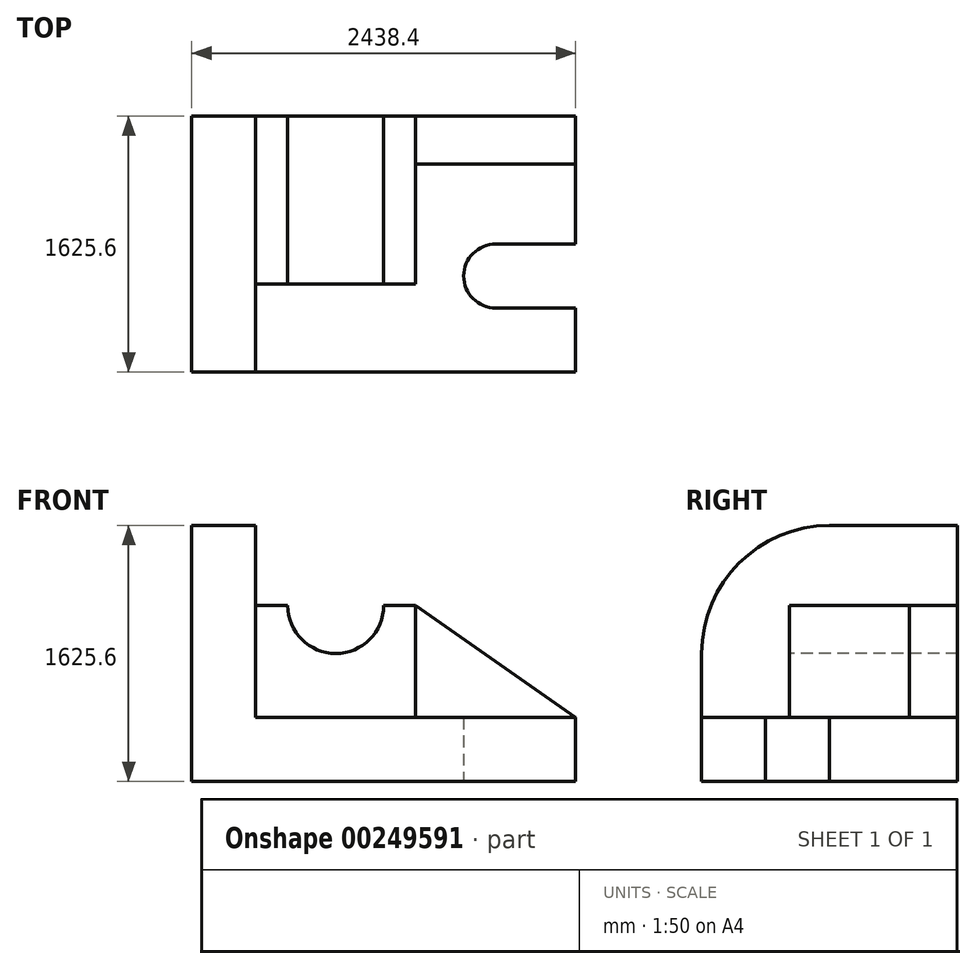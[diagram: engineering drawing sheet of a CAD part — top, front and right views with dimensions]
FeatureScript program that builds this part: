
annotation { "Feature Type Name" : "Feature", "Feature Type Description" : "" }
export const myFeature = defineFeature(function(context is Context, id is Id, definition is map)
    precondition{}
    {
        {
            var Q0;
            Q0=qCreatedBy(makeId("Top.planeOp"),FACE);
            var sketch = newSketch(context, id + "F0", { "sketchPlane" : qUnion([Q0])});
            skLineSegment(sketch, "E0.bottom", {"start": v(0, 0) * mm, "end": v(-2438.4, 0) * mm});
            skLineSegment(sketch, "E0.top", {"start": v(0, 1625.6) * mm, "end": v(-2438.4, 1625.6) * mm});
            skLineSegment(sketch, "E0.left", {"start": v(0, 0) * mm, "end": v(0, 1625.6) * mm});
            skLineSegment(sketch, "E0.right", {"start": v(-2438.4, 0) * mm, "end": v(-2438.4, 1625.6) * mm});
            skLineSegment(sketch, "E1", {"start": v(0, 0) * mm, "end": v(0, 406.4) * mm});
            skLineSegment(sketch, "E2", {"start": v(0, 406.4) * mm, "end": v(-508, 406.4) * mm});
            skLineSegment(sketch, "E3", {"start": v(-508, 812.8) * mm, "end": v(0, 812.8) * mm});
            skArc(sketch, "E4", {"start": v(-508, 812.8) * mm, "mid": v(-711.2, 609.6) * mm, "end": v(-508, 406.4) * mm});
            skLineSegment(sketch, "E5.bottom", {"start": v(0, 1625.6) * mm, "end": v(-863.6, 1625.6) * mm});
            skLineSegment(sketch, "E5.left", {"start": v(0, 1625.6) * mm, "end": v(0, 1320.8) * mm});
            skSolve(sketch);
        }
        {
            var Q0;
            Q0=makeQuery(id+"F0.imprint","IMPRINT",FACE,{"disambiguationData":[TD([[makeQuery(id+"F0.imprint","IMPRINT",EDGE,{"derivedFrom":sQuery(id+"F0.wireOp",EDGE,"E0.bottom")}),-1.0]])]});
            extrude(context, id + "F1", {"entities" : qUnion([Q0]), "depth" : 406.4 * mm});
        }
        {
            var Q0;
            Q0=makeQuery(id+"F1.opExtrude","CAP_FACE",FACE,{"disambiguationData":[OSD([sQuery(id+"F0.wireOp",EDGE,"E0.bottom"),sQuery(id+"F0.wireOp",EDGE,"E0.top"),sQuery(id+"F0.wireOp",EDGE,"E0.left"),sQuery(id+"F0.wireOp",EDGE,"E0.right"),sQuery(id+"F0.wireOp",EDGE,"E1"),sQuery(id+"F0.wireOp",EDGE,"E2"),sQuery(id+"F0.wireOp",EDGE,"E3"),sQuery(id+"F0.wireOp",EDGE,"E4"),sQuery(id+"F0.wireOp",EDGE,"E5.bottom"),sQuery(id+"F0.wireOp",EDGE,"E5.left")])],"isStart":false});
            var sketch = newSketch(context, id + "F2", { "sketchPlane" : qUnion([Q0])});
            skLineSegment(sketch, "E6.bottom", {"start": v(-2438.4, 0) * mm, "end": v(-2032, 0) * mm});
            skLineSegment(sketch, "E6.top", {"start": v(-2438.4, 1625.6) * mm, "end": v(-2032, 1625.6) * mm});
            skLineSegment(sketch, "E6.left", {"start": v(-2438.4, 0) * mm, "end": v(-2438.4, 1625.6) * mm});
            skLineSegment(sketch, "E6.right", {"start": v(-2032, 0) * mm, "end": v(-2032, 1625.6) * mm});
            skSolve(sketch);
        }
        {
            var Q0;
            Q0=makeQuery(id+"F2.imprint","IMPRINT",FACE,{"disambiguationData":[TD([[makeQuery(id+"F2.imprint","IMPRINT",EDGE,{"derivedFrom":sQuery(id+"F2.wireOp",EDGE,"E6.bottom")}),-1.0]])]});
            extrude(context, id + "F3", {"entities" : qUnion([Q0]), "operationType" : NewBodyOperationType.ADD, "depth" : 1219.2 * mm});
        }
        {
            var Q0;
            Q0=makeQuery(id+"F3.opExtrude","CAP_EDGE",EDGE,{"disambiguationData":[OSD([sQuery(id+"F2.wireOp",EDGE,"E6.bottom")])],"isStart":false});
            fillet(context, id + "F4", {"entities" : qUnion([Q0]), "radius" : 812.8 * mm, "tangentPropagation" : true, "allowEdgeOverflow" : false});
        }
        {
            var Q0;
            Q0=makeQuery(id+"F1.opExtrude","CAP_FACE",FACE,{"disambiguationData":[OSD([sQuery(id+"F0.wireOp",EDGE,"E0.bottom"),sQuery(id+"F0.wireOp",EDGE,"E0.top"),sQuery(id+"F0.wireOp",EDGE,"E0.left"),sQuery(id+"F0.wireOp",EDGE,"E0.right"),sQuery(id+"F0.wireOp",EDGE,"E1"),sQuery(id+"F0.wireOp",EDGE,"E2"),sQuery(id+"F0.wireOp",EDGE,"E3"),sQuery(id+"F0.wireOp",EDGE,"E4"),sQuery(id+"F0.wireOp",EDGE,"E5.bottom"),sQuery(id+"F0.wireOp",EDGE,"E5.left")])],"isStart":false});
            var sketch = newSketch(context, id + "F5", { "sketchPlane" : qUnion([Q0])});
            skLineSegment(sketch, "E7.bottom", {"start": v(-2032, 1625.6) * mm, "end": v(-1016, 1625.6) * mm});
            skLineSegment(sketch, "E7.top", {"start": v(-2032, 558.8) * mm, "end": v(-1016, 558.8) * mm});
            skLineSegment(sketch, "E7.left", {"start": v(-2032, 1625.6) * mm, "end": v(-2032, 558.8) * mm});
            skLineSegment(sketch, "E7.right", {"start": v(-1016, 1625.6) * mm, "end": v(-1016, 558.8) * mm});
            skSolve(sketch);
        }
        {
            var Q0;
            Q0=makeQuery(id+"F5.imprint","IMPRINT",FACE,{"disambiguationData":[TD([[makeQuery(id+"F5.imprint","IMPRINT",EDGE,{"derivedFrom":sQuery(id+"F5.wireOp",EDGE,"E7.bottom")}),1.0]])]});
            extrude(context, id + "F6", {"entities" : qUnion([Q0]), "operationType" : NewBodyOperationType.ADD, "depth" : 711.2 * mm});
        }
        {
            var Q0;
            Q0=makeQuery(id+"F6.opExtrude","SWEPT_FACE",FACE,{"disambiguationData":[OSD([sQuery(id+"F5.wireOp",EDGE,"E7.top")])]});
            var sketch = newSketch(context, id + "F7", { "sketchPlane" : qUnion([Q0])});
            skLineSegment(sketch, "E8", {"start": v(-1016, 1117.6) * mm, "end": v(-1524, 1117.6) * mm});
            skCircle(sketch, "E9", {"center": v(-1524, 1117.6) * mm, "radius": 304.8 * mm});
            skSolve(sketch);
        }
        {
            var Q0;
            {var subQ0=sQuery(id+"F7.wireOp",EDGE,"E8");var subQ1=makeQuery(id+"F6.opExtrude","CAP_EDGE",EDGE,{"disambiguationData":[OSD([sQuery(id+"F5.wireOp",EDGE,"E7.top")])],"isStart":false});var subQ2=makeQuery(id+"F7.imprint","INTERSECT",VERTEX,{"derivedFrom":[subQ1,subQ0]});Q0=makeQuery(id+"F7.imprint","IMPRINT",FACE,{"disambiguationData":[TD([[makeQuery(id+"F7.imprint","IMPRINT",EDGE,{"disambiguationData":[TD([[subQ2,-1.0]])],"derivedFrom":subQ0}),1.0]])]});}
            var Q1;
            {var subQ0=sQuery(id+"F7.wireOp",EDGE,"E8");var subQ1=makeQuery(id+"F6.opExtrude","CAP_EDGE",EDGE,{"disambiguationData":[OSD([sQuery(id+"F5.wireOp",EDGE,"E7.top")])],"isStart":false});var subQ2=makeQuery(id+"F7.imprint","INTERSECT",VERTEX,{"derivedFrom":[subQ1,subQ0]});Q1=makeQuery(id+"F7.imprint","IMPRINT",FACE,{"disambiguationData":[TD([[makeQuery(id+"F7.imprint","IMPRINT",EDGE,{"disambiguationData":[TD([[subQ2,-1.0]])],"derivedFrom":subQ0}),-1.0]])]});}
            extrude(context, id + "F8", {"entities" : qUnion([Q0, Q1]), "operationType" : NewBodyOperationType.REMOVE, "oppositeDirection" : true, "depth" : 1066.8 * mm});
        }
        {
            var Q0;
            Q0=makeQuery(id+"F1.opExtrude","CAP_FACE",FACE,{"disambiguationData":[OSD([sQuery(id+"F0.wireOp",EDGE,"E0.bottom"),sQuery(id+"F0.wireOp",EDGE,"E0.top"),sQuery(id+"F0.wireOp",EDGE,"E0.left"),sQuery(id+"F0.wireOp",EDGE,"E0.right"),sQuery(id+"F0.wireOp",EDGE,"E1"),sQuery(id+"F0.wireOp",EDGE,"E2"),sQuery(id+"F0.wireOp",EDGE,"E3"),sQuery(id+"F0.wireOp",EDGE,"E4"),sQuery(id+"F0.wireOp",EDGE,"E5.bottom"),sQuery(id+"F0.wireOp",EDGE,"E5.left")])],"isStart":false});
            var sketch = newSketch(context, id + "F9", { "sketchPlane" : qUnion([Q0])});
            skLineSegment(sketch, "E10.bottom", {"start": v(0, 1625.6) * mm, "end": v(-1016, 1625.6) * mm});
            skLineSegment(sketch, "E10.top", {"start": v(0, 1320.8) * mm, "end": v(-1016, 1320.8) * mm});
            skLineSegment(sketch, "E10.left", {"start": v(0, 1625.6) * mm, "end": v(0, 1320.8) * mm});
            skLineSegment(sketch, "E10.right", {"start": v(-1016, 1625.6) * mm, "end": v(-1016, 1320.8) * mm});
            skSolve(sketch);
        }
        {
            var Q0;
            Q0=makeQuery(id+"F9.imprint","IMPRINT",FACE,{"disambiguationData":[TD([[makeQuery(id+"F9.imprint","IMPRINT",EDGE,{"derivedFrom":sQuery(id+"F9.wireOp",EDGE,"E10.bottom")}),1.0]])]});
            extrude(context, id + "F10", {"entities" : qUnion([Q0]), "operationType" : NewBodyOperationType.ADD, "depth" : 711.2 * mm});
        }
        {
            var Q0;
            Q0=makeQuery(id+"F10.opExtrude","CAP_EDGE",EDGE,{"disambiguationData":[OSD([sQuery(id+"F9.wireOp",EDGE,"E10.left")])],"isStart":false});
            chamfer(context, id + "F11", {"entities" : qUnion([Q0]), "chamferType" : ChamferType.TWO_OFFSETS, "width1" : 1016 * mm, "oppositeDirection" : false, "width2" : 711.2 * mm, "tangentPropagation" : true});
        }
    });
